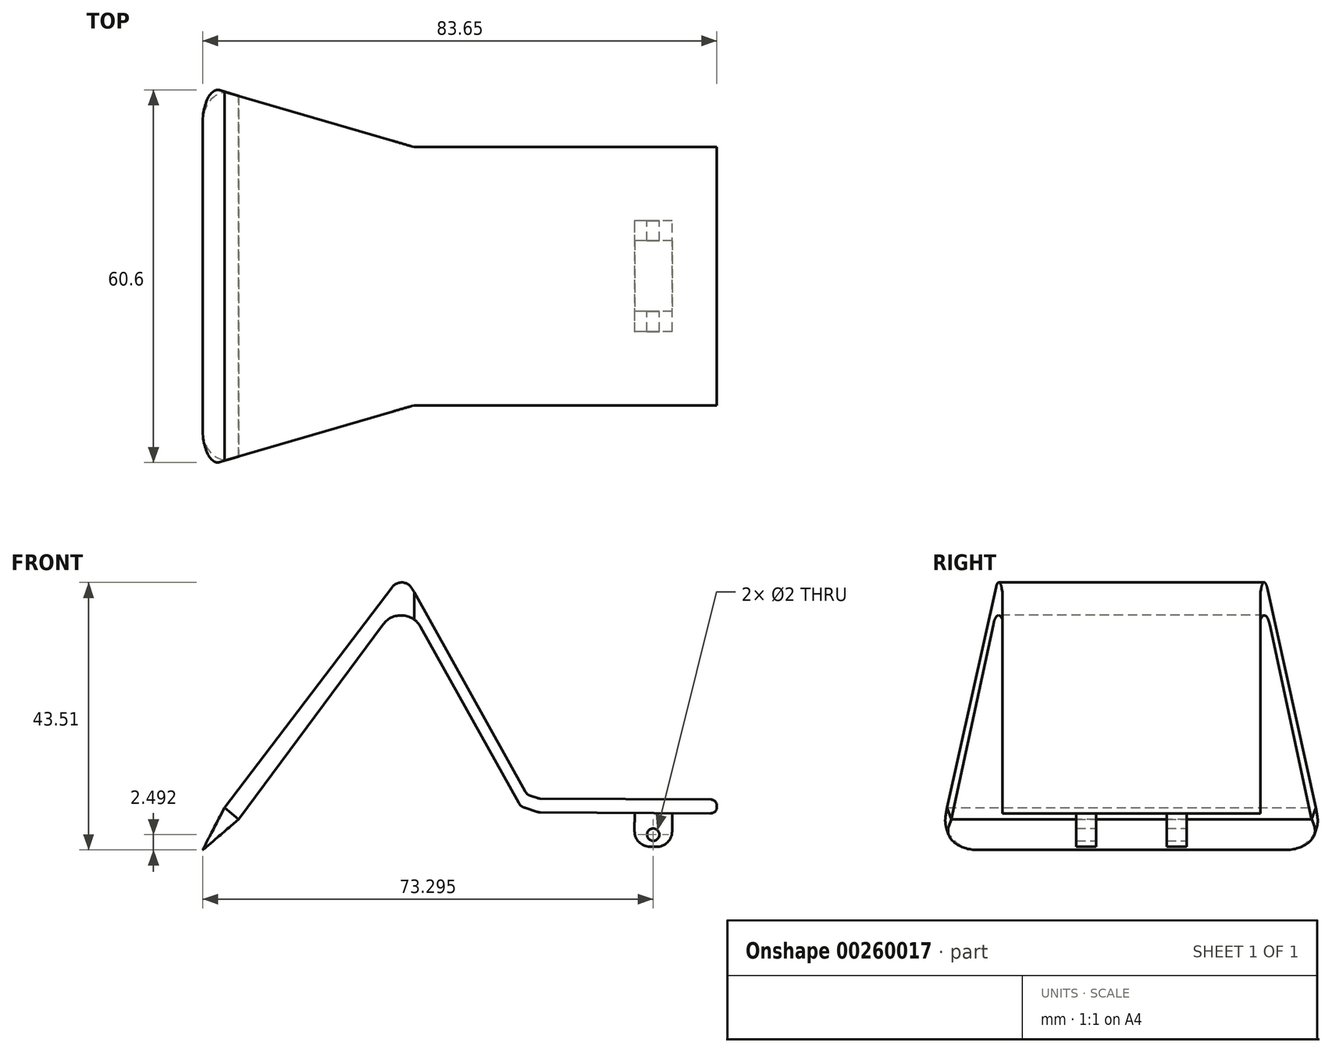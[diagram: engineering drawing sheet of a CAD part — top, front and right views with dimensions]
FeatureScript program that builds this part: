
annotation { "Feature Type Name" : "Feature", "Feature Type Description" : "" }
export const myFeature = defineFeature(function(context is Context, id is Id, definition is map)
    precondition{}
    {
        {
            var Q0;
            Q0=qCreatedBy(makeId("Front.planeOp"),FACE);
            var sketch = newSketch(context, id + "F0", { "sketchPlane" : qUnion([Q0])});
            skPoint(sketch, "E0.middle", {"position": v(0.2, 4.07) * mm});
            skLineSegment(sketch, "E1", {"start": v(-50.55, 0.25) * mm, "end": v(-21.48, 38.44) * mm});
            skLineSegment(sketch, "E2", {"start": v(-21.48, 38.44) * mm, "end": v(-1.34, 2.31) * mm});
            skLineSegment(sketch, "E3", {"start": v(0.53, 1.7) * mm, "end": v(-1.34, 2.31) * mm});
            skLineSegment(sketch, "E4", {"start": v(0.53, 1.7) * mm, "end": v(29.55, 1.54) * mm});
            skLineSegment(sketch, "E5.0", {"start": v(0.54, -0.54) * mm, "end": v(29.54, -0.7) * mm});
            skLineSegment(sketch, "E5.1", {"start": v(0.54, -0.54) * mm, "end": v(-2.38, 0.4) * mm});
            skLineSegment(sketch, "E5.2", {"start": v(-21.42, 34.55) * mm, "end": v(-2.38, 0.4) * mm});
            skLineSegment(sketch, "E5.3", {"start": v(-48.24, -1.67) * mm, "end": v(-21.42, 34.55) * mm});
            skLineSegment(sketch, "E6", {"start": v(-48.24, -1.67) * mm, "end": v(-50.55, 0.25) * mm});
            skLineSegment(sketch, "E7", {"start": v(29.55, 1.54) * mm, "end": v(29.54, -0.7) * mm});
            skSolve(sketch);
        }
        {
            var Q0;
            Q0=makeQuery(id+"F0.imprint","IMPRINT",FACE,{"disambiguationData":[TD([[makeQuery(id+"F0.imprint","IMPRINT",EDGE,{"derivedFrom":sQuery(id+"F0.wireOp",EDGE,"E1")}),-1.0]])]});
            extrude(context, id + "F1", {"entities" : qUnion([Q0]), "endBound" : BoundingType.SYMMETRIC, "depth" : 60 * mm});
        }
        {
            var Q0;
            Q0=makeQuery(id+"F1.opExtrude","SWEPT_EDGE",EDGE,{"disambiguationData":[OSD([sQuery(id+"F0.wireOp",EDGE,"E1"),sQuery(id+"F0.wireOp",EDGE,"E2")])]});
            fillet(context, id + "F2", {"entities" : qUnion([Q0]), "radius" : 1.94 * mm, "tangentPropagation" : true, "allowEdgeOverflow" : false});
        }
        {
            var Q0;
            Q0=makeQuery(id+"F1.opExtrude","SWEPT_EDGE",EDGE,{"disambiguationData":[OSD([sQuery(id+"F0.wireOp",EDGE,"E5.2"),sQuery(id+"F0.wireOp",EDGE,"E5.3")])]});
            fillet(context, id + "F3", {"entities" : qUnion([Q0]), "radius" : 3.63 * mm, "tangentPropagation" : true, "allowEdgeOverflow" : false});
        }
        {
            var Q0;
            Q0=makeQuery(id+"F1.opExtrude","SWEPT_EDGE",EDGE,{"disambiguationData":[OSD([sQuery(id+"F0.wireOp",EDGE,"E5.1"),sQuery(id+"F0.wireOp",EDGE,"E5.2")])]});
            var Q1;
            Q1=makeQuery(id+"F1.opExtrude","SWEPT_EDGE",EDGE,{"disambiguationData":[OSD([sQuery(id+"F0.wireOp",EDGE,"E5.0"),sQuery(id+"F0.wireOp",EDGE,"E5.1")])]});
            var Q2;
            Q2=makeQuery(id+"F1.opExtrude","SWEPT_EDGE",EDGE,{"disambiguationData":[OSD([sQuery(id+"F0.wireOp",EDGE,"E2"),sQuery(id+"F0.wireOp",EDGE,"E3")])]});
            var Q3;
            Q3=makeQuery(id+"F1.opExtrude","SWEPT_EDGE",EDGE,{"disambiguationData":[OSD([sQuery(id+"F0.wireOp",EDGE,"E3"),sQuery(id+"F0.wireOp",EDGE,"E4")])]});
            fillet(context, id + "F4", {"entities" : qUnion([Q0, Q1, Q2, Q3]), "radius" : 1.68 * mm, "allowEdgeOverflow" : false});
        }
        {
            var Q0;
            Q0=makeQuery(id+"F1.opExtrude","SWEPT_FACE",FACE,{"disambiguationData":[OSD([sQuery(id+"F0.wireOp",EDGE,"E5.0")])]});
            var sketch = newSketch(context, id + "F5", { "sketchPlane" : qUnion([Q0])});
            skLineSegment(sketch, "E8.bottom", {"start": v(22.27, 9) * mm, "end": v(16.17, 9) * mm});
            skLineSegment(sketch, "E8.top", {"start": v(22.27, -9) * mm, "end": v(16.17, -9) * mm});
            skLineSegment(sketch, "E8.left", {"start": v(22.27, 9) * mm, "end": v(22.27, -9) * mm});
            skLineSegment(sketch, "E8.right", {"start": v(16.17, 9) * mm, "end": v(16.17, -9) * mm});
            skPoint(sketch, "E8.middle", {"position": v(19.22, 0) * mm});
            skSolve(sketch);
        }
        {
            var Q0;
            Q0=makeQuery(id+"F5.imprint","IMPRINT",FACE,{"disambiguationData":[TD([[makeQuery(id+"F5.imprint","IMPRINT",EDGE,{"derivedFrom":sQuery(id+"F5.wireOp",EDGE,"E8.bottom")}),1.0]])]});
            extrude(context, id + "F6", {"entities" : qUnion([Q0]), "operationType" : NewBodyOperationType.ADD, "depth" : 5.5 * mm});
        }
        {
            var Q0;
            Q0=makeQuery(id+"F6.opExtrude","CAP_EDGE",EDGE,{"disambiguationData":[OSD([sQuery(id+"F5.wireOp",EDGE,"E8.right")])],"isStart":false});
            var Q1;
            Q1=makeQuery(id+"F6.opExtrude","CAP_EDGE",EDGE,{"disambiguationData":[OSD([sQuery(id+"F5.wireOp",EDGE,"E8.left")])],"isStart":false});
            fillet(context, id + "F7", {"entities" : qUnion([Q0, Q1]), "radius" : 2.53 * mm, "tangentPropagation" : true, "allowEdgeOverflow" : false});
        }
        {
            var Q0;
            Q0=qCreatedBy(makeId("Front.planeOp"),FACE);
            var sketch = newSketch(context, id + "F8", { "sketchPlane" : qUnion([Q0])});
            skCircle(sketch, "E9", {"center": v(19.18, -4.17) * mm, "radius": 1 * mm});
            skSolve(sketch);
        }
        {
            var Q0;
            Q0=qSketchRegion(id+"F8",true);
            extrude(context, id + "F9", {"entities" : qUnion([Q0]), "operationType" : NewBodyOperationType.REMOVE, "endBound" : BoundingType.SYMMETRIC, "depth" : 25 * mm});
        }
        {
            var Q0;
            Q0=qCreatedBy(makeId("Right.planeOp"),FACE);
            var sketch = newSketch(context, id + "F10", { "sketchPlane" : qUnion([Q0])});
            skLineSegment(sketch, "E10.bottom", {"start": v(-5.75, -0.72) * mm, "end": v(5.75, -0.72) * mm});
            skLineSegment(sketch, "E10.top", {"start": v(-5.75, -6.16) * mm, "end": v(5.75, -6.16) * mm});
            skLineSegment(sketch, "E10.left", {"start": v(-5.75, -0.72) * mm, "end": v(-5.75, -6.16) * mm});
            skLineSegment(sketch, "E10.right", {"start": v(5.75, -0.72) * mm, "end": v(5.75, -6.16) * mm});
            skPoint(sketch, "E10.middle", {"position": v(0, -3.44) * mm});
            skSolve(sketch);
        }
        {
            var Q0;
            Q0=makeQuery(id+"F10.imprint","IMPRINT",FACE,{"disambiguationData":[TD([[makeQuery(id+"F10.imprint","IMPRINT",EDGE,{"derivedFrom":sQuery(id+"F10.wireOp",EDGE,"E10.bottom")}),-1.0]])]});
            extrude(context, id + "F11", {"entities" : qUnion([Q0]), "operationType" : NewBodyOperationType.REMOVE, "depth" : 30.5 * mm});
        }
        {
            var Q0;
            Q0=makeQuery(id+"F1.opExtrude","SWEPT_EDGE",EDGE,{"disambiguationData":[OSD([sQuery(id+"F0.wireOp",EDGE,"E4"),sQuery(id+"F0.wireOp",EDGE,"E7")])]});
            var Q1;
            Q1=makeQuery(id+"F1.opExtrude","SWEPT_EDGE",EDGE,{"disambiguationData":[OSD([sQuery(id+"F0.wireOp",EDGE,"E5.0"),sQuery(id+"F0.wireOp",EDGE,"E7")])]});
            fillet(context, id + "F12", {"entities" : qUnion([Q0, Q1]), "radius" : 1 * mm, "tangentPropagation" : true, "allowEdgeOverflow" : false});
        }
        {
            var Q0;
            Q0=qCreatedBy(makeId("Front.planeOp"),FACE);
            cPlane(context, id + "F13", {"entities" : qUnion([Q0]), "cplaneType" : CPlaneType.OFFSET, "offset" : 21 * mm, "oppositeDirection" : true, "width" : 150 * mm, "height" : 150 * mm});
        }
        {
            var Q0;
            Q0=qCreatedBy(makeId("Front.planeOp"),FACE);
            cPlane(context, id + "F14", {"entities" : qUnion([Q0]), "cplaneType" : CPlaneType.OFFSET, "offset" : 21 * mm, "width" : 150 * mm, "height" : 150 * mm});
        }
        {
            var Q0;
            Q0=qCreatedBy(makeId("Top.planeOp"),FACE);
            var sketch = newSketch(context, id + "F15", { "sketchPlane" : qUnion([Q0])});
            skLineSegment(sketch, "E11", {"start": v(36.18, -21) * mm, "end": v(-19.7, -21) * mm});
            skLineSegment(sketch, "E12", {"start": v(-19.7, -21) * mm, "end": v(-50.8, -30.07) * mm});
            skLineSegment(sketch, "E13", {"start": v(-50.8, -30.07) * mm, "end": v(36.65, -30.07) * mm});
            skLineSegment(sketch, "E14", {"start": v(36.65, -30.07) * mm, "end": v(36.18, -21) * mm});
            skLineSegment(sketch, "E15.MirrorCS", {"start": v(36.18, 21) * mm, "end": v(-19.7, 21) * mm});
            skLineSegment(sketch, "E16.MirrorCS", {"start": v(-19.7, 21) * mm, "end": v(-50.8, 30.07) * mm});
            skLineSegment(sketch, "E17.MirrorCS", {"start": v(-50.8, 30.07) * mm, "end": v(36.65, 30.07) * mm});
            skLineSegment(sketch, "E18.MirrorCS", {"start": v(36.65, 30.07) * mm, "end": v(36.18, 21) * mm});
            skSolve(sketch);
        }
        {
            var Q0;
            Q0=makeQuery(id+"F15.imprint","IMPRINT",FACE,{"disambiguationData":[TD([[makeQuery(id+"F15.imprint","IMPRINT",EDGE,{"derivedFrom":sQuery(id+"F15.wireOp",EDGE,"E11")}),1.0]])]});
            var Q1;
            Q1=makeQuery(id+"F15.imprint","IMPRINT",FACE,{"disambiguationData":[TD([[makeQuery(id+"F15.imprint","IMPRINT",EDGE,{"derivedFrom":sQuery(id+"F15.wireOp",EDGE,"E15.MirrorCS")}),-1.0]])]});
            extrude(context, id + "F16", {"entities" : qUnion([Q0, Q1]), "operationType" : NewBodyOperationType.REMOVE, "endBound" : BoundingType.SYMMETRIC, "depth" : 103.2 * mm});
        }
        {
            var Q0;
            Q0=makeQuery(id+"F1.opExtrude","SWEPT_FACE",FACE,{"disambiguationData":[OSD([sQuery(id+"F0.wireOp",EDGE,"E6")])]});
            var sketch = newSketch(context, id + "F17", { "sketchPlane" : qUnion([Q0])});
            skLineSegment(sketch, "E19.0.0", {"start": v(-36.05, -29.32) * mm, "end": v(-36.05, 29.32) * mm});
            skLineSegment(sketch, "E19.0.1", {"start": v(-36.05, 29.32) * mm, "end": v(-39.05, 30) * mm});
            skLineSegment(sketch, "E19.0.2", {"start": v(-39.05, 30) * mm, "end": v(-39.05, -30) * mm});
            skLineSegment(sketch, "E19.0.3", {"start": v(-39.05, -30) * mm, "end": v(-36.05, -29.32) * mm});
            skSolve(sketch);
        }
        {
            var Q0;
            Q0=makeQuery(id+"F17.imprint","IMPRINT",FACE,{"disambiguationData":[TD([[makeQuery(id+"F17.imprint","IMPRINT",EDGE,{"derivedFrom":sQuery(id+"F17.wireOp",EDGE,"E19.0.0")}),-1.0]])]});
            extrude(context, id + "F18", {"entities" : qUnion([Q0]), "depth" : 7.6 * mm, "hasDraft" : true, "draftAngle" : 0.2 * radian});
        }
        {
            var Q0;
            Q0=makeQuery(id+"F18.opExtrude","CAP_EDGE",EDGE,{"disambiguationData":[OSD([sQuery(id+"F17.wireOp",EDGE,"E19.0.3")])],"isStart":false});
            var Q1;
            Q1=makeQuery(id+"F18.opExtrude","CAP_EDGE",EDGE,{"disambiguationData":[OSD([sQuery(id+"F17.wireOp",EDGE,"E19.0.1")])],"isStart":false});
            fillet(context, id + "F19", {"entities" : qUnion([Q0, Q1]), "radius" : 5 * mm, "tangentPropagation" : true, "allowEdgeOverflow" : false});
        }
        {
            var Q0;
            Q0=qCreatedBy(id+"F13.planeOp",FACE);
            var sketch = newSketch(context, id + "F20", { "sketchPlane" : qUnion([Q0])});
            skLineSegment(sketch, "E20", {"start": v(-50.32, 0.71) * mm, "end": v(-54.11, -6.66) * mm});
            skLineSegment(sketch, "E21", {"start": v(-54.11, -6.66) * mm, "end": v(-47.87, -1.36) * mm});
            skLineSegment(sketch, "E22", {"start": v(-47.87, -1.36) * mm, "end": v(-44.99, -4.85) * mm});
            skLineSegment(sketch, "E23", {"start": v(-44.99, -4.85) * mm, "end": v(-52.2, -10.32) * mm});
            skLineSegment(sketch, "E24", {"start": v(-52.2, -10.32) * mm, "end": v(-57.62, -5.04) * mm});
            skLineSegment(sketch, "E25", {"start": v(-57.62, -5.04) * mm, "end": v(-53.9, 1.36) * mm});
            skLineSegment(sketch, "E26", {"start": v(-53.9, 1.36) * mm, "end": v(-50.32, 0.71) * mm});
            skSolve(sketch);
        }
        {
            var Q0;
            Q0=makeQuery(id+"F20.imprint","IMPRINT",FACE,{"disambiguationData":[TD([[makeQuery(id+"F20.imprint","IMPRINT",EDGE,{"derivedFrom":sQuery(id+"F20.wireOp",EDGE,"E20")}),-1.0]])]});
            extrude(context, id + "F21", {"entities" : qUnion([Q0]), "operationType" : NewBodyOperationType.REMOVE, "endBound" : BoundingType.SYMMETRIC, "depth" : 131.8 * mm});
        }
    });
